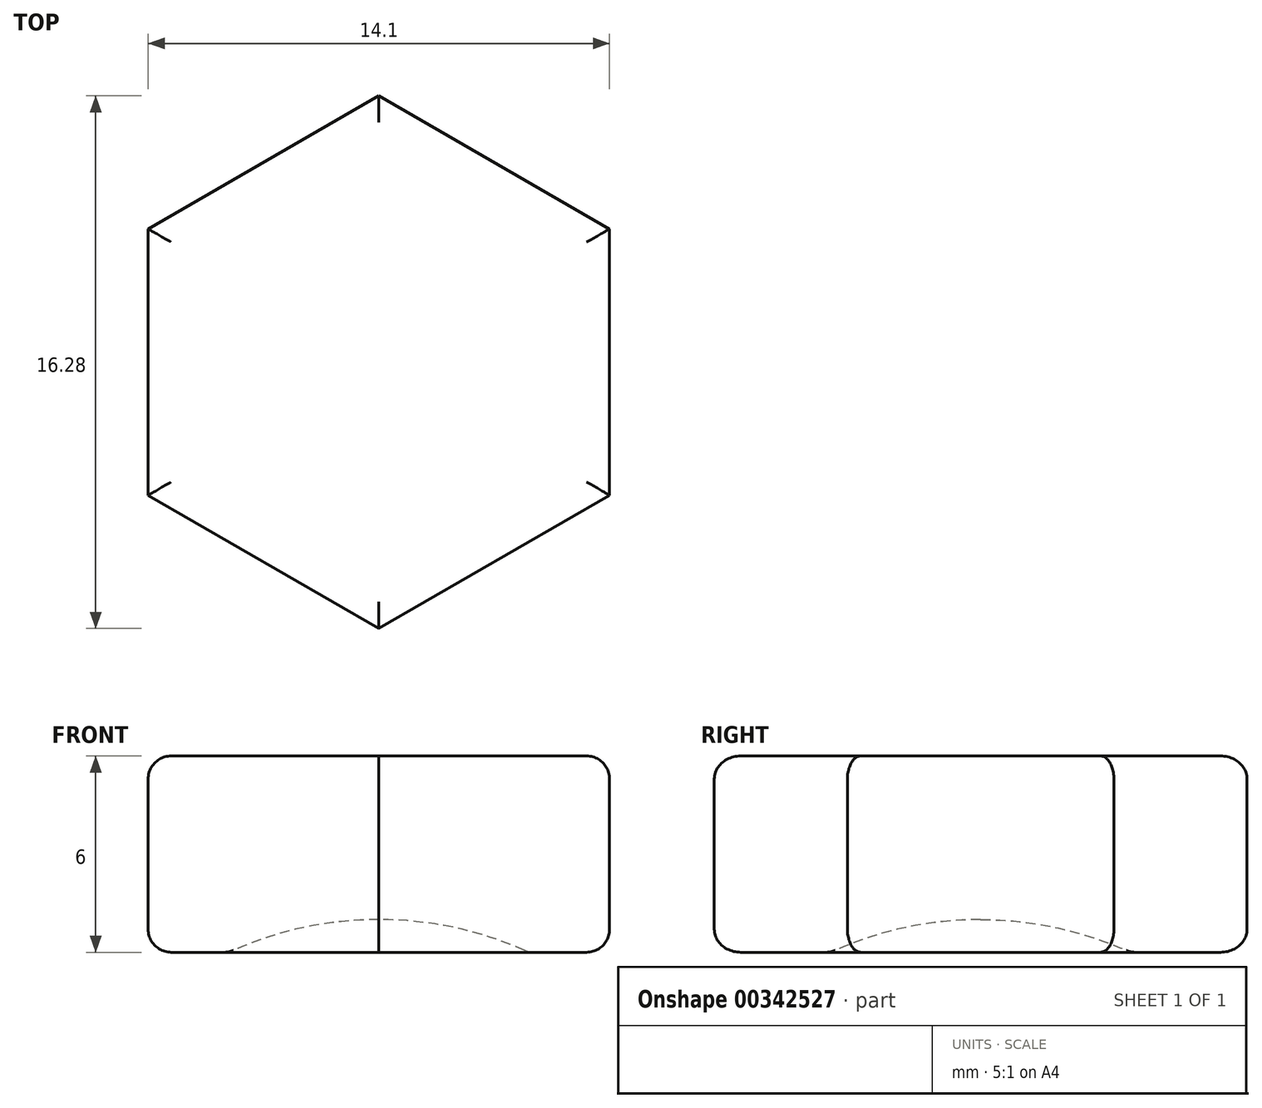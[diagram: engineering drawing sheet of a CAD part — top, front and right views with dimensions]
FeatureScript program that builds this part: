
annotation { "Feature Type Name" : "Feature", "Feature Type Description" : "" }
export const myFeature = defineFeature(function(context is Context, id is Id, definition is map)
    precondition{}
    {
        {
            var Q0;
            Q0=qCreatedBy(makeId("Top.planeOp"),FACE);
            var sketch = newSketch(context, id + "F0", { "sketchPlane" : qUnion([Q0])});
            skCircle(sketch, "E0.cCircle", {"center": v(0, 0) * mm, "radius": 8.14 * mm, "construction": true});
            skLineSegment(sketch, "E0.0", {"start": v(7.05, 4.07) * mm, "end": v(7.05, -4.07) * mm});
            skLineSegment(sketch, "E0.1", {"start": v(7.05, -4.07) * mm, "end": v(0, -8.14) * mm});
            skLineSegment(sketch, "E0.2", {"start": v(0, -8.14) * mm, "end": v(-7.05, -4.07) * mm});
            skLineSegment(sketch, "E0.3", {"start": v(-7.05, -4.07) * mm, "end": v(-7.05, 4.07) * mm});
            skLineSegment(sketch, "E0.4", {"start": v(-7.05, 4.07) * mm, "end": v(0, 8.14) * mm});
            skLineSegment(sketch, "E0.5", {"start": v(0, 8.14) * mm, "end": v(7.05, 4.07) * mm});
            skSolve(sketch);
        }
        {
            var Q0;
            Q0=qSketchRegion(id+"F0",true);
            extrude(context, id + "F1", {"entities" : qUnion([Q0]), "depth" : 6 * mm});
        }
        {
            var Q0;
            Q0=qCreatedBy(makeId("Right.planeOp"),FACE);
            var sketch = newSketch(context, id + "F2", { "sketchPlane" : qUnion([Q0])});
            skLineSegment(sketch, "E1", {"start": v(0, 0) * mm, "end": v(0, -10) * mm});
            skArc(sketch, "E2", {"start": v(0, 1) * mm, "mid": v(-11, -10) * mm, "end": v(0, -21) * mm});
            skLineSegment(sketch, "E3", {"start": v(0, -10) * mm, "end": v(0, -21) * mm});
            skLineSegment(sketch, "E4", {"start": v(0, 0) * mm, "end": v(0, 1) * mm});
            skSolve(sketch);
        }
        {
            var Q0;
            Q0=qSketchRegion(id+"F2",true);
            var Q1;
            Q1=sQuery(id+"F2.wireOp",EDGE,"E1");
            revolve(context, id + "F3", {"operationType" : NewBodyOperationType.REMOVE, "entities" : qUnion([Q0]), "axis" : qUnion([Q1]), "revolveType" : RevolveType.FULL, "oppositeDirection" : true});
        }
        {
            var Q0;
            Q0=makeQuery(id+"F1.opExtrude","CAP_FACE",FACE,{"disambiguationData":[OSD([sQuery(id+"F0.wireOp",EDGE,"E0.0"),sQuery(id+"F0.wireOp",EDGE,"E0.1"),sQuery(id+"F0.wireOp",EDGE,"E0.2"),sQuery(id+"F0.wireOp",EDGE,"E0.3"),sQuery(id+"F0.wireOp",EDGE,"E0.4"),sQuery(id+"F0.wireOp",EDGE,"E0.5")])],"isStart":false});
            var Q1;
            Q1=makeQuery(id+"F1.opExtrude","CAP_FACE",FACE,{"disambiguationData":[OSD([sQuery(id+"F0.wireOp",EDGE,"E0.0"),sQuery(id+"F0.wireOp",EDGE,"E0.1"),sQuery(id+"F0.wireOp",EDGE,"E0.2"),sQuery(id+"F0.wireOp",EDGE,"E0.3"),sQuery(id+"F0.wireOp",EDGE,"E0.4"),sQuery(id+"F0.wireOp",EDGE,"E0.5")])],"isStart":true});
            fillet(context, id + "F4", {"entities" : qUnion([Q0, Q1]), "radius" : 0.7 * mm, "tangentPropagation" : true, "allowEdgeOverflow" : false});
        }
    });
